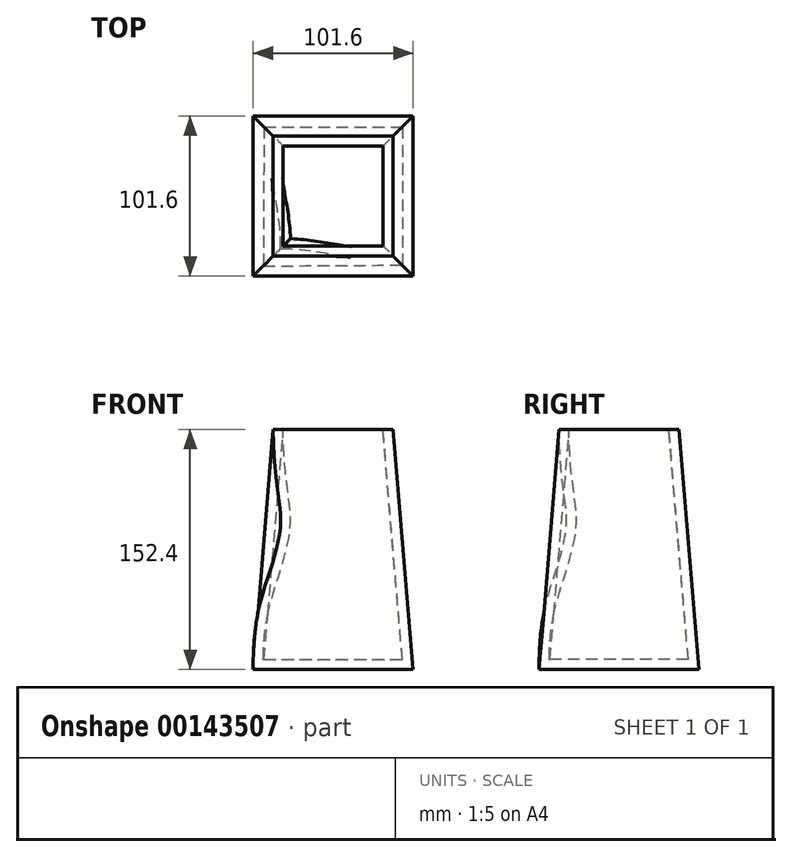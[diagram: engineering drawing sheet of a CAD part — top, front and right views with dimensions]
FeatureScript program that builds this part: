
annotation { "Feature Type Name" : "Feature", "Feature Type Description" : "" }
export const myFeature = defineFeature(function(context is Context, id is Id, definition is map)
    precondition{}
    {
        {
            var Q0;
            Q0=qCreatedBy(makeId("Top.planeOp"),FACE);
            var sketch = newSketch(context, id + "F0", { "sketchPlane" : qUnion([Q0])});
            skLineSegment(sketch, "E0.bottom", {"start": v(-50.8, 50.8) * mm, "end": v(50.8, 50.8) * mm});
            skLineSegment(sketch, "E0.top", {"start": v(-50.8, -50.8) * mm, "end": v(50.8, -50.8) * mm});
            skLineSegment(sketch, "E0.left", {"start": v(-50.8, 50.8) * mm, "end": v(-50.8, -50.8) * mm});
            skLineSegment(sketch, "E0.right", {"start": v(50.8, 50.8) * mm, "end": v(50.8, -50.8) * mm});
            skPoint(sketch, "E0.middle", {"position": v(0, 0) * mm});
            skSolve(sketch);
        }
        {
            var Q0;
            Q0=qCreatedBy(makeId("Top.planeOp"),FACE);
            cPlane(context, id + "F1", {"entities" : qUnion([Q0]), "cplaneType" : CPlaneType.OFFSET, "offset" : 152.4 * mm, "width" : 152.4 * mm, "height" : 152.4 * mm});
        }
        {
            var Q0;
            Q0=qCreatedBy(id+"F1.planeOp",FACE);
            var sketch = newSketch(context, id + "F2", { "sketchPlane" : qUnion([Q0])});
            skLineSegment(sketch, "E1.bottom", {"start": v(-38.1, 38.1) * mm, "end": v(38.1, 38.1) * mm});
            skLineSegment(sketch, "E1.top", {"start": v(-38.1, -38.1) * mm, "end": v(38.1, -38.1) * mm});
            skLineSegment(sketch, "E1.left", {"start": v(-38.1, 38.1) * mm, "end": v(-38.1, -38.1) * mm});
            skLineSegment(sketch, "E1.right", {"start": v(38.1, 38.1) * mm, "end": v(38.1, -38.1) * mm});
            skPoint(sketch, "E1.middle", {"position": v(0, 0) * mm});
            skSolve(sketch);
        }
        {
            var Q0;
            Q0=qCreatedBy(makeId("Front.planeOp"),FACE);
            var sketch = newSketch(context, id + "F3", { "sketchPlane" : qUnion([Q0])});
            skLineSegment(sketch, "E2", {"start": v(0, 0) * mm, "end": v(0, 154.85) * mm});
            skSolve(sketch);
        }
        {
            var Q0;
            Q0=qCreatedBy(makeId("Front.planeOp"),FACE);
            var Q1;
            Q1=sQuery(id+"F3.wireOp",EDGE,"E2");
            cPlane(context, id + "F4", {"entities" : qUnion([Q0, Q1]), "cplaneType" : CPlaneType.LINE_ANGLE, "offset" : 25.4 * mm, "angle" : 45 * degree, "width" : 152.4 * mm, "height" : 152.4 * mm});
        }
        {
            var Q0;
            Q0=qCreatedBy(id+"F4.planeOp",FACE);
            var sketch = newSketch(context, id + "F5", { "sketchPlane" : qUnion([Q0])});
            skFitSpline(sketch, "E3", {"points": [v(71.84, 0) * mm, v(63.81, 46.64) * mm, v(47.35, 90.46) * mm, v(53.88, 152.4) * mm], "startDerivative": vector(0, 184.92) * mm, "endDerivative": vector(0, 284.07) * mm});
            skLineSegment(sketch, "E4", {"start": v(71.84, 0) * mm, "end": v(71.84, 40.2) * mm, "construction": true});
            skLineSegment(sketch, "E5", {"start": v(53.88, 152.4) * mm, "end": v(53.88, 122.06) * mm, "construction": true});
            skSolve(sketch);
        }
        {
            var Q0;
            Q0=makeQuery(id+"F0.imprint","IMPRINT",FACE,{"disambiguationData":[TD([[makeQuery(id+"F0.imprint","IMPRINT",EDGE,{"derivedFrom":sQuery(id+"F0.wireOp",EDGE,"E0.bottom")}),-1.0]])]});
            var Q1;
            Q1=makeQuery(id+"F2.imprint","IMPRINT",FACE,{"disambiguationData":[TD([[makeQuery(id+"F2.imprint","IMPRINT",EDGE,{"derivedFrom":sQuery(id+"F2.wireOp",EDGE,"E1.bottom")}),-1.0]])]});
            var Q2;
            Q2=sQuery(id+"F5.wireOp",EDGE,"E3");
            var Q3;
            Q3=sQuery(id+"FAcPCVkNzMoNvUX_0.1.F5.wireOp",EDGE,"E3");
            var Q4;
            Q4=sQuery(id+"FAcPCVkNzMoNvUX_0.3.F5.wireOp",EDGE,"E3");
            var Q5;
            Q5=sQuery(id+"FAcPCVkNzMoNvUX_0.2.F5.wireOp",EDGE,"E3");
            loft(context, id + "F6", {"addGuides" : true, "sheetProfilesArray" : [{ "sheetProfileEntities" : qUnion([Q0]) }, { "sheetProfileEntities" : qUnion([Q1]) }], "guidesArray" : [{ "guideEntities" : qUnion([Q2]), "guideDerivativeType" : LoftGuideDerivativeType.DEFAULT, "guideDerivativeMagnitude" : 1 }, { "guideEntities" : qUnion([Q3]), "guideDerivativeType" : LoftGuideDerivativeType.DEFAULT, "guideDerivativeMagnitude" : 1 }, { "guideEntities" : qUnion([Q4]), "guideDerivativeType" : LoftGuideDerivativeType.DEFAULT, "guideDerivativeMagnitude" : 1 }, { "guideEntities" : qUnion([Q5]), "guideDerivativeType" : LoftGuideDerivativeType.DEFAULT, "guideDerivativeMagnitude" : 1 }]});
        }
        {
            var Q0;
            Q0=makeQuery(id+"F6.opLoft","CAP_FACE",FACE,{"disambiguationData":[OSD([makeQuery(id+"F2.imprint","IMPRINT",FACE,{"disambiguationData":[TD([[makeQuery(id+"F2.imprint","IMPRINT",EDGE,{"derivedFrom":sQuery(id+"F2.wireOp",EDGE,"E1.bottom")}),-1.0]])]})])],"isStart":true});
            shell(context, id + "F7", {"entities" : qUnion([Q0]), "thickness" : 6.35 * mm});
        }
    });
